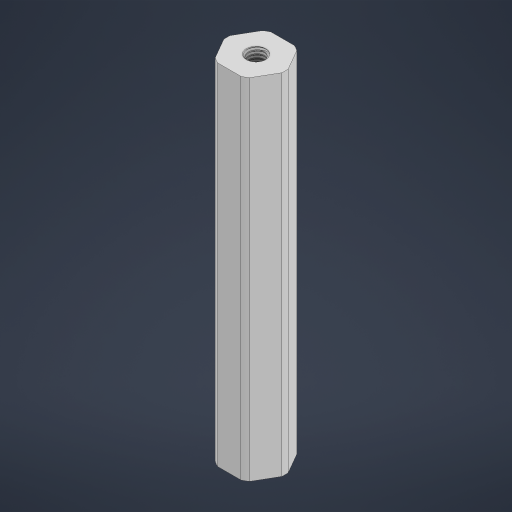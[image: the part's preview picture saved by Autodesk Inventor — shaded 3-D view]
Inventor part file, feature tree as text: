
AUTODESK INVENTOR PART (.ipt)
format: ipt  version: 2023 (Build 270158000, 158)  size: 1,019,904 bytes
history: native  units: in
note: dims shown in document units (in); Inventor stores cm internally (conversion verified against a paired STEP export)
features: mirror x1
ambient origin geometry x8: Origin, YZ Plane, XZ Plane, XY Plane, X Axis, Y Axis, Z Axis, Center Point
bodies: Solid1 (feature_tree)
feature tree (1):
  mirror  "Mirror2"
